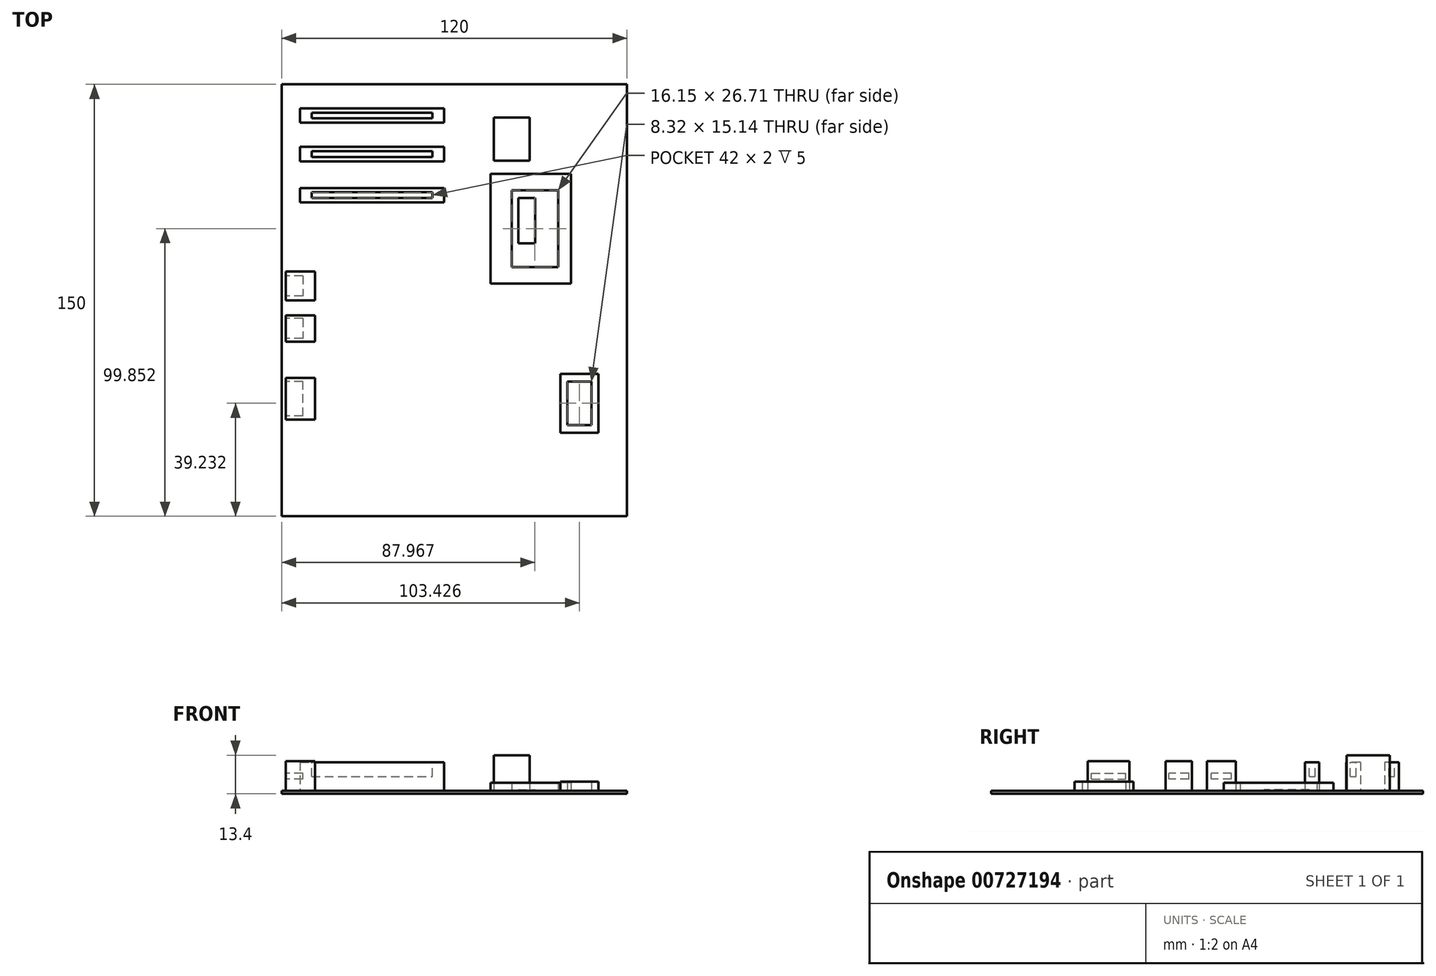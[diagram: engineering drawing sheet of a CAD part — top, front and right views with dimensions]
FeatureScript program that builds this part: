
annotation { "Feature Type Name" : "Feature", "Feature Type Description" : "" }
export const myFeature = defineFeature(function(context is Context, id is Id, definition is map)
    precondition{}
    {
        {
            var Q0;
            Q0=qCreatedBy(makeId("Top.planeOp"),FACE);
            var sketch = newSketch(context, id + "F0", { "sketchPlane" : qUnion([Q0])});
            skLineSegment(sketch, "E0.bottom", {"start": v(-60, -75) * mm, "end": v(60, -75) * mm});
            skLineSegment(sketch, "E0.top", {"start": v(-60, 75) * mm, "end": v(60, 75) * mm});
            skLineSegment(sketch, "E0.left", {"start": v(-60, -75) * mm, "end": v(-60, 75) * mm});
            skLineSegment(sketch, "E0.right", {"start": v(60, -75) * mm, "end": v(60, 75) * mm});
            skPoint(sketch, "E0.middle", {"position": v(0, 0) * mm});
            skSolve(sketch);
        }
        {
            var Q0;
            Q0 = qSketchRegion(id + "F0", true);
            extrude(context, id + "F1", {"entities" : qUnion([Q0]), "depth" : 1 * mm, "offsetDistance" : 25 * mm});
        }
        {
            var Q0;
            Q0=makeQuery(id+"F1.opExtrude","CAP_FACE",FACE,{"disambiguationData":[OSD([sQuery(id+"F0.wireOp",EDGE,"E0.bottom"),sQuery(id+"F0.wireOp",EDGE,"E0.top"),sQuery(id+"F0.wireOp",EDGE,"E0.left"),sQuery(id+"F0.wireOp",EDGE,"E0.right")])],"isStart":false});
            var sketch = newSketch(context, id + "F2", { "sketchPlane" : qUnion([Q0])});
            skLineSegment(sketch, "E1.bottom", {"start": v(-53.6, 66.66) * mm, "end": v(-3.6, 66.66) * mm});
            skLineSegment(sketch, "E1.top", {"start": v(-53.6, 61.66) * mm, "end": v(-3.6, 61.66) * mm});
            skLineSegment(sketch, "E1.left", {"start": v(-53.6, 66.66) * mm, "end": v(-53.6, 61.66) * mm});
            skLineSegment(sketch, "E1.right", {"start": v(-3.6, 66.66) * mm, "end": v(-3.6, 61.66) * mm});
            skLineSegment(sketch, "E2.bottom", {"start": v(-53.6, 53.28) * mm, "end": v(-3.6, 53.28) * mm});
            skLineSegment(sketch, "E2.top", {"start": v(-53.6, 48.28) * mm, "end": v(-3.6, 48.28) * mm});
            skLineSegment(sketch, "E2.left", {"start": v(-53.6, 53.28) * mm, "end": v(-53.6, 48.28) * mm});
            skLineSegment(sketch, "E2.right", {"start": v(-3.6, 53.28) * mm, "end": v(-3.6, 48.28) * mm});
            skLineSegment(sketch, "E3.bottom", {"start": v(-53.6, 39) * mm, "end": v(-3.6, 39) * mm});
            skLineSegment(sketch, "E3.top", {"start": v(-53.6, 34) * mm, "end": v(-3.6, 34) * mm});
            skLineSegment(sketch, "E3.left", {"start": v(-53.6, 39) * mm, "end": v(-53.6, 34) * mm});
            skLineSegment(sketch, "E3.right", {"start": v(-3.6, 39) * mm, "end": v(-3.6, 34) * mm});
            skPoint(sketch, "E4.end.orphan", {"position": v(-53.6, 40.61) * mm});
            skLineSegment(sketch, "E5.trimOffspring", {"start": v(-53.6, 40.61) * mm, "end": v(-53.6, 34) * mm});
            skSolve(sketch);
        }
        {
            var Q0;
            Q0 = qSketchRegion(id + "F2", true);
            extrude(context, id + "F3", {"entities" : qUnion([Q0]), "depth" : 10 * mm, "offsetDistance" : 25 * mm});
        }
        {
            var Q0;
            Q0=makeQuery(id+"F3.opExtrude","CAP_FACE",FACE,{"disambiguationData":[OSD([sQuery(id+"F2.wireOp",EDGE,"E1.bottom"),sQuery(id+"F2.wireOp",EDGE,"E1.top"),sQuery(id+"F2.wireOp",EDGE,"E1.right"),sQuery(id+"F2.wireOp",EDGE,"E1.left")])],"isStart":false});
            var sketch = newSketch(context, id + "F4", { "sketchPlane" : qUnion([Q0])});
            skLineSegment(sketch, "E6.bottom", {"start": v(-49.6, 63.16) * mm, "end": v(-7.6, 63.16) * mm});
            skLineSegment(sketch, "E6.top", {"start": v(-49.6, 65.16) * mm, "end": v(-7.6, 65.16) * mm});
            skLineSegment(sketch, "E6.left", {"start": v(-49.6, 63.16) * mm, "end": v(-49.6, 65.16) * mm});
            skLineSegment(sketch, "E6.right", {"start": v(-7.6, 63.16) * mm, "end": v(-7.6, 65.16) * mm});
            skPoint(sketch, "E6.middle", {"position": v(-28.6, 64.16) * mm});
            skPoint(sketch, "E6.middle.positionSnap0", {"position": v(-3.6, 64.16) * mm});
            skPoint(sketch, "E6.middle.positionSnap1", {"position": v(-28.6, 61.66) * mm});
            skPoint(sketch, "E6.centerSnap0", {"position": v(-3.6, 64.16) * mm});
            skPoint(sketch, "E6.centerSnap1", {"position": v(-28.6, 61.66) * mm});
            skSolve(sketch);
        }
        {
            var Q0;
            Q0 = qSketchRegion(id + "F4", true);
            extrude(context, id + "F5", {"entities" : qUnion([Q0]), "oppositeDirection" : true, "depth" : 5 * mm, "offsetDistance" : 25 * mm});
        }
        {
            var Q0;
            Q0=makeQuery(id+"F3.opExtrude","CAP_FACE",FACE,{"disambiguationData":[OSD([sQuery(id+"F2.wireOp",EDGE,"E2.bottom"),sQuery(id+"F2.wireOp",EDGE,"E2.top"),sQuery(id+"F2.wireOp",EDGE,"E2.right"),sQuery(id+"F2.wireOp",EDGE,"E2.left")])],"isStart":false});
            var sketch = newSketch(context, id + "F6", { "sketchPlane" : qUnion([Q0])});
            skLineSegment(sketch, "E7.bottom", {"start": v(-49.6, 49.78) * mm, "end": v(-7.6, 49.78) * mm});
            skLineSegment(sketch, "E7.top", {"start": v(-49.6, 51.78) * mm, "end": v(-7.6, 51.78) * mm});
            skLineSegment(sketch, "E7.left", {"start": v(-49.6, 49.78) * mm, "end": v(-49.6, 51.78) * mm});
            skLineSegment(sketch, "E7.right", {"start": v(-7.6, 49.78) * mm, "end": v(-7.6, 51.78) * mm});
            skPoint(sketch, "E7.middle", {"position": v(-28.6, 50.78) * mm});
            skPoint(sketch, "E7.middle.positionSnap0", {"position": v(-3.6, 50.78) * mm});
            skPoint(sketch, "E7.middle.positionSnap1", {"position": v(-28.6, 53.28) * mm});
            skPoint(sketch, "E7.centerSnap0", {"position": v(-3.6, 50.78) * mm});
            skPoint(sketch, "E7.centerSnap1", {"position": v(-28.6, 53.28) * mm});
            skSolve(sketch);
        }
        {
            var Q0;
            Q0 = qSketchRegion(id + "F6", true);
            extrude(context, id + "F7", {"entities" : qUnion([Q0]), "oppositeDirection" : true, "depth" : 5 * mm, "offsetDistance" : 25 * mm});
        }
        {
            var Q0;
            Q0=makeQuery(id+"F3.opExtrude","CAP_FACE",FACE,{"disambiguationData":[OSD([sQuery(id+"F2.wireOp",EDGE,"E3.bottom"),sQuery(id+"F2.wireOp",EDGE,"E3.top"),sQuery(id+"F2.wireOp",EDGE,"E3.right"),sQuery(id+"F2.wireOp",EDGE,"E5.trimOffspring")])],"isStart":false});
            var sketch = newSketch(context, id + "F8", { "sketchPlane" : qUnion([Q0])});
            skLineSegment(sketch, "E8.bottom", {"start": v(-49.6, 35.5) * mm, "end": v(-7.6, 35.5) * mm});
            skLineSegment(sketch, "E8.top", {"start": v(-49.6, 37.5) * mm, "end": v(-7.6, 37.5) * mm});
            skLineSegment(sketch, "E8.left", {"start": v(-49.6, 35.5) * mm, "end": v(-49.6, 37.5) * mm});
            skLineSegment(sketch, "E8.right", {"start": v(-7.6, 35.5) * mm, "end": v(-7.6, 37.5) * mm});
            skPoint(sketch, "E8.middle", {"position": v(-28.6, 36.5) * mm});
            skPoint(sketch, "E8.middle.positionSnap0", {"position": v(-3.6, 36.5) * mm});
            skPoint(sketch, "E8.middle.positionSnap1", {"position": v(-28.6, 39) * mm});
            skPoint(sketch, "E8.centerSnap0", {"position": v(-3.6, 36.5) * mm});
            skPoint(sketch, "E8.centerSnap1", {"position": v(-28.6, 39) * mm});
            skSolve(sketch);
        }
        {
            var Q0;
            Q0 = qSketchRegion(id + "F8", true);
            extrude(context, id + "F9", {"entities" : qUnion([Q0]), "operationType" : NewBodyOperationType.REMOVE, "oppositeDirection" : true, "depth" : 5 * mm, "offsetDistance" : 25 * mm});
        }
        {
            var Q0;
            Q0=makeQuery(id+"F1.opExtrude","CAP_FACE",FACE,{"disambiguationData":[OSD([sQuery(id+"F0.wireOp",EDGE,"E0.bottom"),sQuery(id+"F0.wireOp",EDGE,"E0.top"),sQuery(id+"F0.wireOp",EDGE,"E0.left"),sQuery(id+"F0.wireOp",EDGE,"E0.right")])],"isStart":false});
            var sketch = newSketch(context, id + "F10", { "sketchPlane" : qUnion([Q0])});
            skSolve(sketch);
        }
        {
            var Q0;
            Q0=makeQuery(id+"F10.imprint","IMPRINT",FACE,{"disambiguationData":[TD([[makeQuery(id+"F10.imprint","IMPRINT",EDGE,{"derivedFrom":makeQuery(id+"F1.opExtrude","CAP_EDGE",EDGE,{"disambiguationData":[OSD([sQuery(id+"F0.wireOp",EDGE,"E0.bottom")])],"isStart":false})}),1.0]])]});
            var sketch = newSketch(context, id + "F11", { "sketchPlane" : qUnion([Q0])});
            skLineSegment(sketch, "E9.bottom", {"start": v(26.2, 63.41) * mm, "end": v(13.65, 63.41) * mm});
            skLineSegment(sketch, "E9.top", {"start": v(26.2, 48.43) * mm, "end": v(13.65, 48.43) * mm});
            skLineSegment(sketch, "E9.left", {"start": v(26.2, 63.41) * mm, "end": v(26.2, 48.43) * mm});
            skLineSegment(sketch, "E9.right", {"start": v(13.65, 63.41) * mm, "end": v(13.65, 48.43) * mm});
            skSolve(sketch);
        }
        {
            var Q0;
            Q0=makeQuery(id+"F11.imprint","IMPRINT",FACE,{"disambiguationData":[TD([[makeQuery(id+"F11.imprint","IMPRINT",EDGE,{"derivedFrom":sQuery(id+"F11.wireOp",EDGE,"E9.bottom")}),1.0]])]});
            extrude(context, id + "F12", {"entities" : qUnion([Q0]), "depth" : 12.4 * mm, "offsetDistance" : 25 * mm});
        }
        {
            var Q0;
            Q0=makeQuery(id+"F10.imprint","IMPRINT",FACE,{"disambiguationData":[TD([[makeQuery(id+"F10.imprint","IMPRINT",EDGE,{"derivedFrom":makeQuery(id+"F1.opExtrude","CAP_EDGE",EDGE,{"disambiguationData":[OSD([sQuery(id+"F0.wireOp",EDGE,"E0.bottom")])],"isStart":false})}),1.0]])]});
            var sketch = newSketch(context, id + "F13", { "sketchPlane" : qUnion([Q0])});
            skLineSegment(sketch, "E10.bottom", {"start": v(19.9, 38.2) * mm, "end": v(36.04, 38.2) * mm});
            skLineSegment(sketch, "E10.top", {"start": v(19.9, 11.5) * mm, "end": v(36.04, 11.5) * mm});
            skLineSegment(sketch, "E10.left", {"start": v(19.9, 38.2) * mm, "end": v(19.9, 11.5) * mm});
            skLineSegment(sketch, "E10.right", {"start": v(36.04, 38.2) * mm, "end": v(36.04, 11.5) * mm});
            skLineSegment(sketch, "E11.bottom", {"start": v(40.51, 43.9) * mm, "end": v(12.58, 43.9) * mm});
            skLineSegment(sketch, "E11.top", {"start": v(40.51, 5.8) * mm, "end": v(12.58, 5.8) * mm});
            skLineSegment(sketch, "E11.left", {"start": v(40.51, 43.9) * mm, "end": v(40.51, 5.8) * mm});
            skLineSegment(sketch, "E11.right", {"start": v(12.58, 43.9) * mm, "end": v(12.58, 5.8) * mm});
            skSolve(sketch);
        }
        {
            var Q0;
            Q0=makeQuery(id+"F13.imprint","IMPRINT",FACE,{"disambiguationData":[TD([[makeQuery(id+"F13.imprint","IMPRINT",EDGE,{"derivedFrom":sQuery(id+"F13.wireOp",EDGE,"E10.bottom")}),1.0]])]});
            extrude(context, id + "F14", {"entities" : qUnion([Q0]), "depth" : 2.8 * mm, "offsetDistance" : 25 * mm});
        }
        {
            var Q0;
            Q0=makeQuery(id+"F10.imprint","IMPRINT",FACE,{"disambiguationData":[TD([[makeQuery(id+"F10.imprint","IMPRINT",EDGE,{"derivedFrom":makeQuery(id+"F1.opExtrude","CAP_EDGE",EDGE,{"disambiguationData":[OSD([sQuery(id+"F0.wireOp",EDGE,"E0.bottom")])],"isStart":false})}),1.0]])]});
            var sketch = newSketch(context, id + "F15", { "sketchPlane" : qUnion([Q0])});
            skLineSegment(sketch, "E12.bottom", {"start": v(22.17, 35.58) * mm, "end": v(28.07, 35.58) * mm});
            skLineSegment(sketch, "E12.top", {"start": v(22.17, 19.84) * mm, "end": v(28.07, 19.84) * mm});
            skLineSegment(sketch, "E12.left", {"start": v(22.17, 35.58) * mm, "end": v(22.17, 19.84) * mm});
            skLineSegment(sketch, "E12.right", {"start": v(28.07, 35.58) * mm, "end": v(28.07, 19.84) * mm});
            skSolve(sketch);
        }
        {
            var Q0;
            Q0 = qSketchRegion(id + "F15", true);
            extrude(context, id + "F16", {"entities" : qUnion([Q0]), "depth" : 0.5 * mm, "offsetDistance" : 25 * mm});
        }
        {
            var Q0;
            Q0=makeQuery(id+"F10.imprint","IMPRINT",FACE,{"disambiguationData":[TD([[makeQuery(id+"F10.imprint","IMPRINT",EDGE,{"derivedFrom":makeQuery(id+"F1.opExtrude","CAP_EDGE",EDGE,{"disambiguationData":[OSD([sQuery(id+"F0.wireOp",EDGE,"E0.bottom")])],"isStart":false})}),1.0]])]});
            var sketch = newSketch(context, id + "F17", { "sketchPlane" : qUnion([Q0])});
            skLineSegment(sketch, "E13.bottom", {"start": v(-58.58, 0) * mm, "end": v(-48.43, 0) * mm});
            skLineSegment(sketch, "E13.top", {"start": v(-58.58, 10.02) * mm, "end": v(-48.43, 10.02) * mm});
            skLineSegment(sketch, "E13.left", {"start": v(-58.58, 0) * mm, "end": v(-58.58, 10.02) * mm});
            skLineSegment(sketch, "E13.right", {"start": v(-48.43, 0) * mm, "end": v(-48.43, 10.02) * mm});
            skLineSegment(sketch, "E14.bottom", {"start": v(-58.58, -5.2) * mm, "end": v(-48.43, -5.2) * mm});
            skLineSegment(sketch, "E14.top", {"start": v(-58.58, -14.37) * mm, "end": v(-48.43, -14.37) * mm});
            skLineSegment(sketch, "E14.left", {"start": v(-58.58, -5.2) * mm, "end": v(-58.58, -14.37) * mm});
            skLineSegment(sketch, "E14.right", {"start": v(-48.43, -5.2) * mm, "end": v(-48.43, -14.37) * mm});
            skLineSegment(sketch, "E15.bottom", {"start": v(-58.58, -26.93) * mm, "end": v(-48.43, -26.93) * mm});
            skLineSegment(sketch, "E15.top", {"start": v(-58.58, -41.43) * mm, "end": v(-48.43, -41.43) * mm});
            skLineSegment(sketch, "E15.left", {"start": v(-58.58, -26.93) * mm, "end": v(-58.58, -41.43) * mm});
            skLineSegment(sketch, "E15.right", {"start": v(-48.43, -26.93) * mm, "end": v(-48.43, -41.43) * mm});
            skSolve(sketch);
        }
        {
            var Q0;
            Q0 = qSketchRegion(id + "F17", true);
            extrude(context, id + "F18", {"entities" : qUnion([Q0]), "depth" : 10.3 * mm, "offsetDistance" : 25 * mm});
        }
        {
            var Q0;
            Q0=makeQuery(id+"F18.opExtrude","SWEPT_FACE",FACE,{"disambiguationData":[OSD([sQuery(id+"F17.wireOp",EDGE,"E13.left")])]});
            var sketch = newSketch(context, id + "F19", { "sketchPlane" : qUnion([Q0])});
            skLineSegment(sketch, "E16.bottom", {"start": v(-8.51, 5.15) * mm, "end": v(-1.51, 5.15) * mm});
            skLineSegment(sketch, "E16.top", {"start": v(-8.51, 7.15) * mm, "end": v(-1.51, 7.15) * mm});
            skLineSegment(sketch, "E16.left", {"start": v(-8.51, 5.15) * mm, "end": v(-8.51, 7.15) * mm});
            skLineSegment(sketch, "E16.right", {"start": v(-1.51, 5.15) * mm, "end": v(-1.51, 7.15) * mm});
            skPoint(sketch, "E16.middle", {"position": v(-5.01, 6.15) * mm});
            skPoint(sketch, "E16.middle.positionSnap0", {"position": v(0, 6.15) * mm});
            skPoint(sketch, "E16.middle.positionSnap1", {"position": v(-5.01, 11.3) * mm});
            skPoint(sketch, "E16.centerSnap0", {"position": v(0, 6.15) * mm});
            skPoint(sketch, "E16.centerSnap1", {"position": v(-5.01, 11.3) * mm});
            skSolve(sketch);
        }
        {
            var Q0;
            Q0 = qSketchRegion(id + "F19", true);
            extrude(context, id + "F20", {"entities" : qUnion([Q0]), "oppositeDirection" : true, "depth" : 6 * mm, "offsetDistance" : 25 * mm});
        }
        {
            var Q0;
            Q0=makeQuery(id+"F18.opExtrude","SWEPT_FACE",FACE,{"disambiguationData":[OSD([sQuery(id+"F17.wireOp",EDGE,"E14.left")])]});
            var sketch = newSketch(context, id + "F21", { "sketchPlane" : qUnion([Q0])});
            skLineSegment(sketch, "E17.bottom", {"start": v(6.28, 5.15) * mm, "end": v(13.28, 5.15) * mm});
            skLineSegment(sketch, "E17.top", {"start": v(6.28, 7.15) * mm, "end": v(13.28, 7.15) * mm});
            skLineSegment(sketch, "E17.left", {"start": v(6.28, 5.15) * mm, "end": v(6.28, 7.15) * mm});
            skLineSegment(sketch, "E17.right", {"start": v(13.28, 5.15) * mm, "end": v(13.28, 7.15) * mm});
            skPoint(sketch, "E17.middle", {"position": v(9.78, 6.15) * mm});
            skPoint(sketch, "E17.middle.positionSnap0", {"position": v(9.78, 11.3) * mm});
            skPoint(sketch, "E17.middle.positionSnap1", {"position": v(14.37, 6.15) * mm});
            skPoint(sketch, "E17.centerSnap0", {"position": v(9.78, 11.3) * mm});
            skPoint(sketch, "E17.centerSnap1", {"position": v(14.37, 6.15) * mm});
            skSolve(sketch);
        }
        {
            var Q0;
            Q0 = qSketchRegion(id + "F21", true);
            extrude(context, id + "F22", {"entities" : qUnion([Q0]), "oppositeDirection" : true, "depth" : 6 * mm, "offsetDistance" : 25 * mm});
        }
        {
            var Q0;
            Q0=makeQuery(id+"F18.opExtrude","SWEPT_FACE",FACE,{"disambiguationData":[OSD([sQuery(id+"F17.wireOp",EDGE,"E15.left")])]});
            var sketch = newSketch(context, id + "F23", { "sketchPlane" : qUnion([Q0])});
            skLineSegment(sketch, "E18.bottom", {"start": v(40.18, 5.15) * mm, "end": v(28.18, 5.15) * mm});
            skLineSegment(sketch, "E18.top", {"start": v(40.18, 7.15) * mm, "end": v(28.18, 7.15) * mm});
            skLineSegment(sketch, "E18.left", {"start": v(40.18, 5.15) * mm, "end": v(40.18, 7.15) * mm});
            skLineSegment(sketch, "E18.right", {"start": v(28.18, 5.15) * mm, "end": v(28.18, 7.15) * mm});
            skPoint(sketch, "E18.middle", {"position": v(34.18, 6.15) * mm});
            skPoint(sketch, "E18.middle.positionSnap0", {"position": v(34.18, 11.3) * mm});
            skPoint(sketch, "E18.middle.positionSnap1", {"position": v(26.93, 6.15) * mm});
            skPoint(sketch, "E18.centerSnap0", {"position": v(34.18, 11.3) * mm});
            skPoint(sketch, "E18.centerSnap1", {"position": v(26.93, 6.15) * mm});
            skSolve(sketch);
        }
        {
            var Q0;
            Q0 = qSketchRegion(id + "F23", true);
            extrude(context, id + "F24", {"entities" : qUnion([Q0]), "oppositeDirection" : true, "depth" : 6 * mm, "offsetDistance" : 25 * mm});
        }
        {
            var Q0;
            Q0=makeQuery(id+"F10.imprint","IMPRINT",FACE,{"disambiguationData":[TD([[makeQuery(id+"F10.imprint","IMPRINT",EDGE,{"derivedFrom":makeQuery(id+"F1.opExtrude","CAP_EDGE",EDGE,{"disambiguationData":[OSD([sQuery(id+"F0.wireOp",EDGE,"E0.bottom")])],"isStart":false})}),1.0]])]});
            var sketch = newSketch(context, id + "F25", { "sketchPlane" : qUnion([Q0])});
            skLineSegment(sketch, "E19.bottom", {"start": v(39.26, -43.34) * mm, "end": v(47.59, -43.34) * mm});
            skLineSegment(sketch, "E19.top", {"start": v(39.26, -28.2) * mm, "end": v(47.59, -28.2) * mm});
            skLineSegment(sketch, "E19.left", {"start": v(39.26, -43.34) * mm, "end": v(39.26, -28.2) * mm});
            skLineSegment(sketch, "E19.right", {"start": v(47.59, -43.34) * mm, "end": v(47.59, -28.2) * mm});
            skPoint(sketch, "E19.middle", {"position": v(43.43, -35.77) * mm});
            skLineSegment(sketch, "E20.bottom", {"start": v(36.87, -45.98) * mm, "end": v(49.98, -45.98) * mm});
            skLineSegment(sketch, "E20.top", {"start": v(36.87, -25.55) * mm, "end": v(49.98, -25.55) * mm});
            skLineSegment(sketch, "E20.left", {"start": v(36.87, -45.98) * mm, "end": v(36.87, -25.55) * mm});
            skLineSegment(sketch, "E20.right", {"start": v(49.98, -45.98) * mm, "end": v(49.98, -25.55) * mm});
            skSolve(sketch);
        }
        {
            var Q0;
            Q0=makeQuery(id+"F25.imprint","IMPRINT",FACE,{"disambiguationData":[TD([[makeQuery(id+"F25.imprint","IMPRINT",EDGE,{"derivedFrom":sQuery(id+"F25.wireOp",EDGE,"E19.bottom")}),-1.0]])]});
            extrude(context, id + "F26", {"entities" : qUnion([Q0]), "depth" : 3.2 * mm, "offsetDistance" : 25 * mm});
        }
    });
